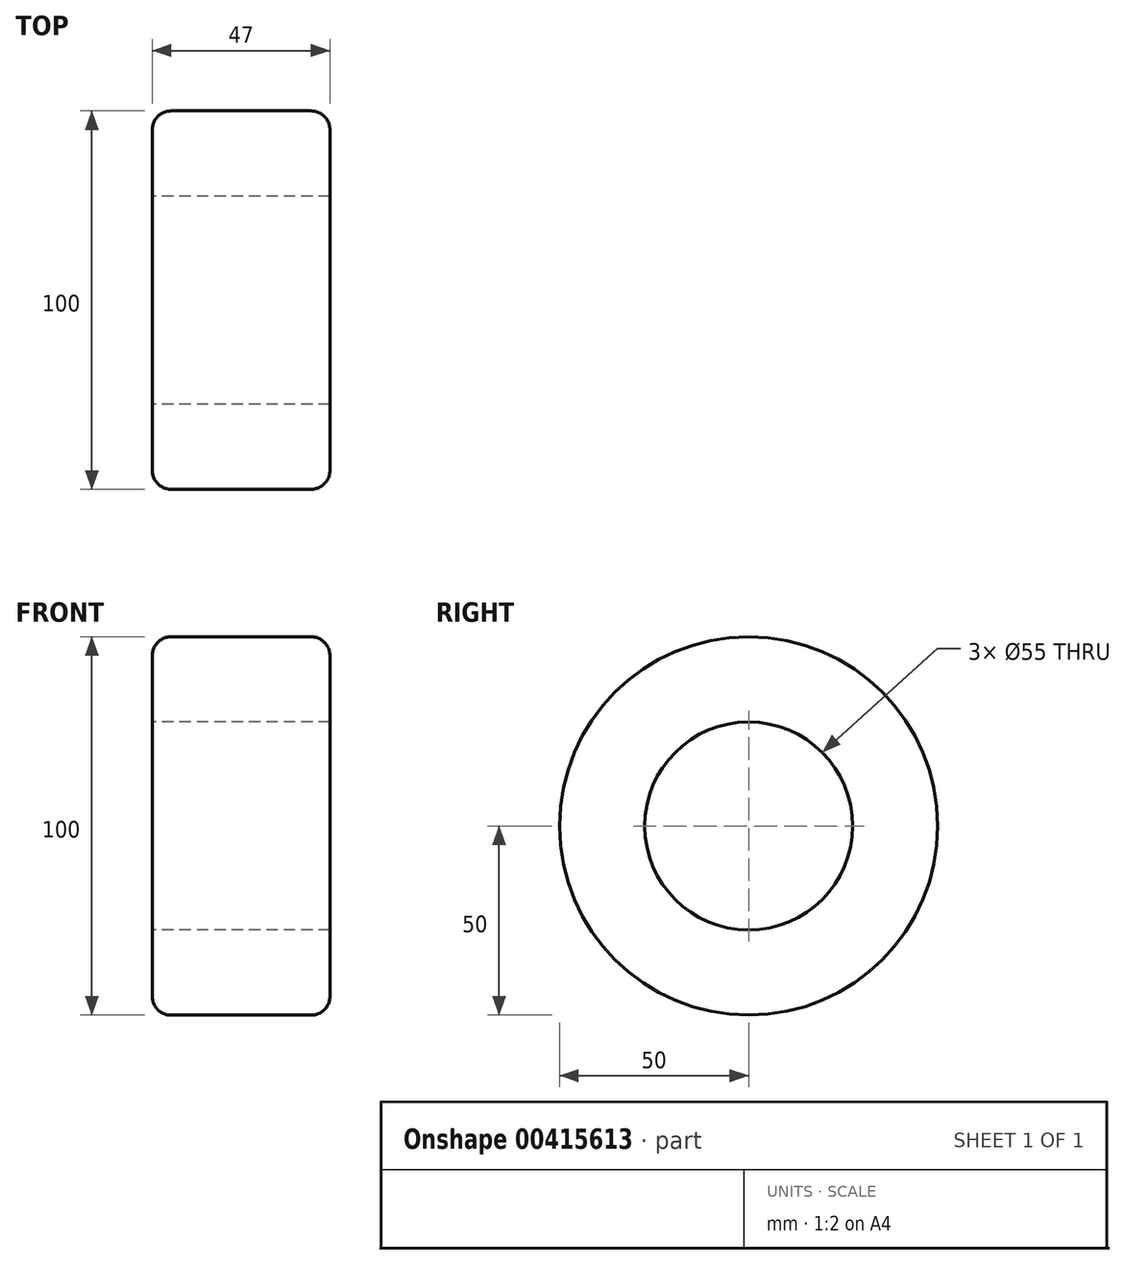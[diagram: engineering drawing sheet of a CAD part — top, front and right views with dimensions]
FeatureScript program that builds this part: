
annotation { "Feature Type Name" : "Feature", "Feature Type Description" : "" }
export const myFeature = defineFeature(function(context is Context, id is Id, definition is map)
    precondition{}
    {
        {
            var Q0;
            Q0=qCreatedBy(makeId("Front.planeOp"),FACE);
            var sketch = newSketch(context, id + "F0", { "sketchPlane" : qUnion([Q0])});
            skLineSegment(sketch, "E0", {"start": v(-23.5, 0) * mm, "end": v(23.5, 0) * mm, "construction": true});
            skLineSegment(sketch, "E1.bottom", {"start": v(-23.5, 27.5) * mm, "end": v(23.5, 27.5) * mm});
            skLineSegment(sketch, "E1.top", {"start": v(-23.5, 50) * mm, "end": v(23.5, 50) * mm});
            skLineSegment(sketch, "E1.left", {"start": v(-23.5, 27.5) * mm, "end": v(-23.5, 50) * mm});
            skLineSegment(sketch, "E1.right", {"start": v(23.5, 27.5) * mm, "end": v(23.5, 50) * mm});
            skSolve(sketch);
        }
        {
            var Q0;
            Q0=makeQuery(id+"F0.imprint","IMPRINT",FACE,{"disambiguationData":[TD([[makeQuery(id+"F0.imprint","IMPRINT",EDGE,{"derivedFrom":sQuery(id+"F0.wireOp",EDGE,"E1.bottom")}),1.0]])]});
            var Q1;
            Q1=sQuery(id+"F0.wireOp",EDGE,"E0");
            revolve(context, id + "F1", {"entities" : qUnion([Q0]), "axis" : qUnion([Q1]), "revolveType" : RevolveType.FULL});
        }
        {
            var Q0;
            Q0=makeQuery(id+"F1.opRevolve","SWEPT_EDGE",EDGE,{"disambiguationData":[OSD([sQuery(id+"F0.wireOp",EDGE,"E1.top"),sQuery(id+"F0.wireOp",EDGE,"E1.right")])]});
            var Q1;
            Q1=makeQuery(id+"F1.opRevolve","SWEPT_EDGE",EDGE,{"disambiguationData":[OSD([sQuery(id+"F0.wireOp",EDGE,"E1.top"),sQuery(id+"F0.wireOp",EDGE,"E1.left")])]});
            fillet(context, id + "F2", {"entities" : qUnion([Q0, Q1]), "radius" : 5 * mm, "tangentPropagation" : true, "allowEdgeOverflow" : false});
        }
    });
